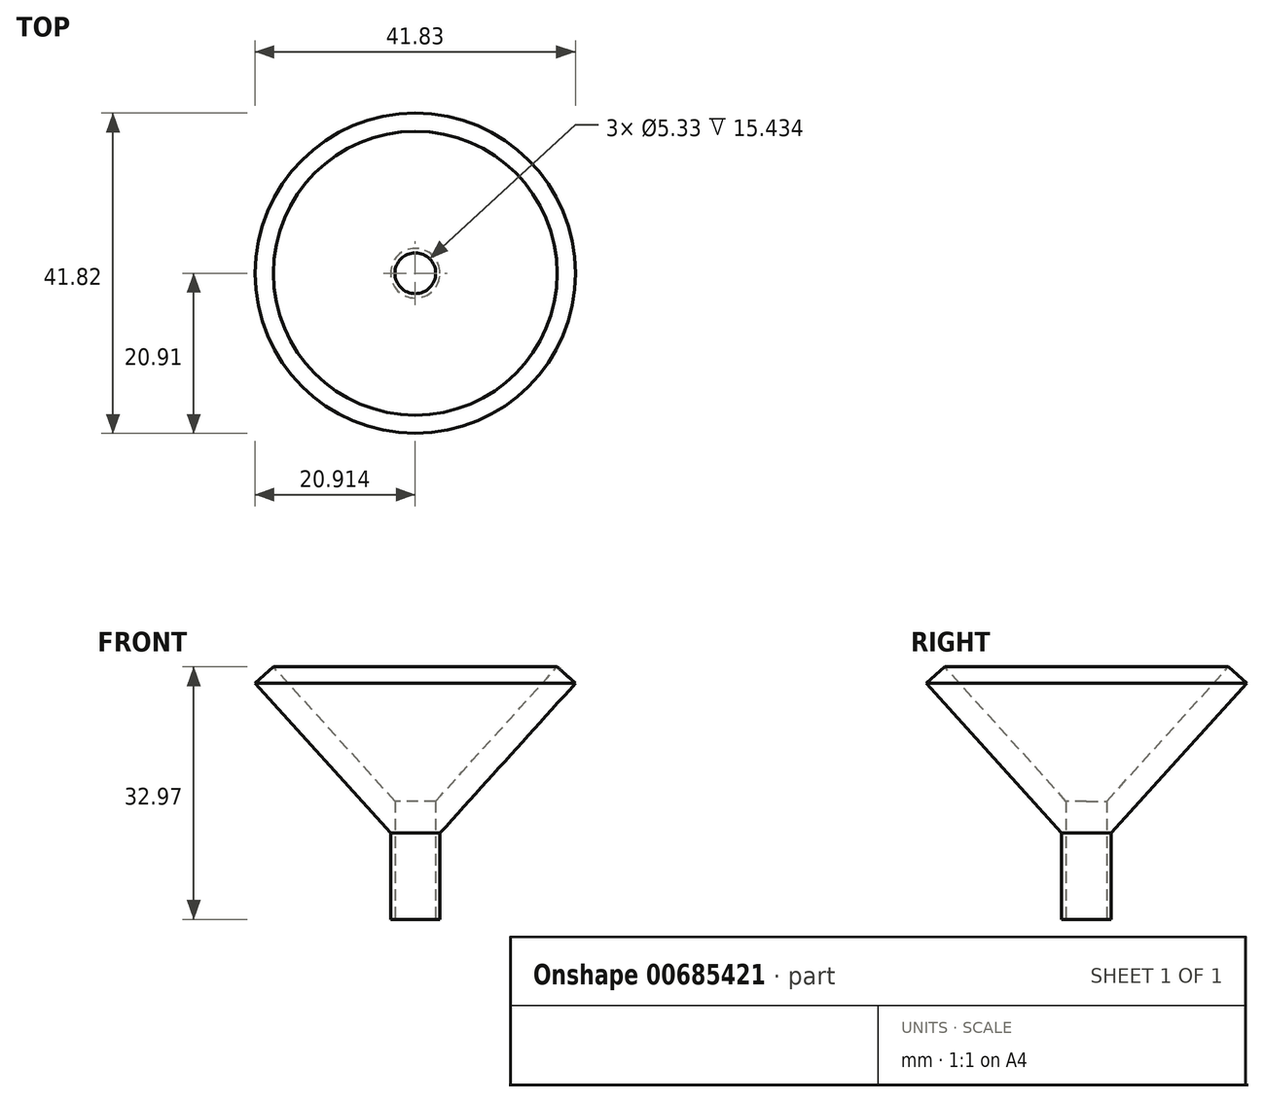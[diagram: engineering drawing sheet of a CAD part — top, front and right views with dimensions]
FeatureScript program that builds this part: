
annotation { "Feature Type Name" : "Feature", "Feature Type Description" : "" }
export const myFeature = defineFeature(function(context is Context, id is Id, definition is map)
    precondition{}
    {
        {
            var Q0;
            Q0=qCreatedBy(makeId("Front.planeOp"),FACE);
            var sketch = newSketch(context, id + "F0", { "sketchPlane" : qUnion([Q0])});
            skLineSegment(sketch, "E0", {"start": v(-39.2, 0) * mm, "end": v(-39.2, 11.28) * mm});
            skLineSegment(sketch, "E1", {"start": v(-39.2, 11.28) * mm, "end": v(-21.51, 30.82) * mm});
            skLineSegment(sketch, "E2", {"start": v(-21.51, 30.82) * mm, "end": v(-23.9, 32.97) * mm});
            skLineSegment(sketch, "E3", {"start": v(-23.9, 32.97) * mm, "end": v(-42.43, 12.5) * mm});
            skLineSegment(sketch, "E4", {"start": v(-42.43, 12.5) * mm, "end": v(-42.43, 0) * mm});
            skLineSegment(sketch, "E5", {"start": v(-42.43, 0) * mm, "end": v(-39.2, 0) * mm});
            skSolve(sketch);
        }
        {
            var Q0;
            Q0=makeQuery(id+"F0.imprint","IMPRINT",FACE,{"disambiguationData":[TD([[makeQuery(id+"F0.imprint","IMPRINT",EDGE,{"derivedFrom":sQuery(id+"F0.wireOp",EDGE,"E0")}),1.0]])]});
            var Q1;
            Q1=sQuery(id+"F0.wireOp",EDGE,"E4");
            revolve(context, id + "F1", {"entities" : qUnion([Q0]), "axis" : qUnion([Q1]), "revolveType" : RevolveType.FULL});
        }
        {
            var Q0;
            Q0=makeQuery(id+"F1.opRevolve","SWEPT_FACE",FACE,{"disambiguationData":[OSD([sQuery(id+"F0.wireOp",EDGE,"E5")])]});
            var sketch = newSketch(context, id + "F2", { "sketchPlane" : qUnion([Q0])});
            skCircle(sketch, "E6", {"center": v(-42.43, 0) * mm, "radius": 2.66 * mm});
            skSolve(sketch);
        }
        {
            var Q0;
            Q0 = qSketchRegion(id + "F2", true);
            extrude(context, id + "F3", {"entities" : qUnion([Q0]), "operationType" : NewBodyOperationType.REMOVE, "oppositeDirection" : true, "depth" : 101.6 * mm, "offsetDistance" : 25.4 * mm});
        }
    });
